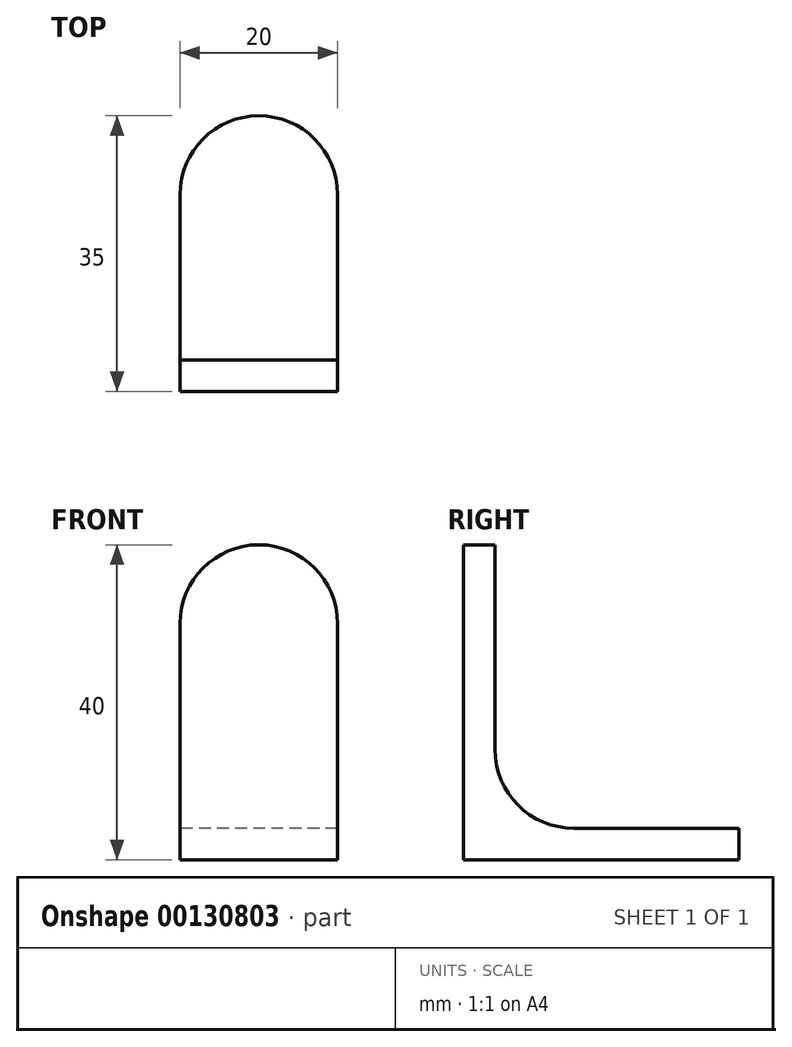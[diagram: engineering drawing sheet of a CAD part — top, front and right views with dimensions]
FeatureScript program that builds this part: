
annotation { "Feature Type Name" : "Feature", "Feature Type Description" : "" }
export const myFeature = defineFeature(function(context is Context, id is Id, definition is map)
    precondition{}
    {
        {
            var Q0;
            Q0=qCreatedBy(makeId("Right.planeOp"),FACE);
            var sketch = newSketch(context, id + "F0", { "sketchPlane" : qUnion([Q0])});
            skLineSegment(sketch, "E0.bottom", {"start": v(0, 0) * mm, "end": v(35, 0) * mm});
            skLineSegment(sketch, "E0.top", {"start": v(0, 4) * mm, "end": v(35, 4) * mm});
            skLineSegment(sketch, "E0.left", {"start": v(0, 0) * mm, "end": v(0, 4) * mm});
            skLineSegment(sketch, "E0.right", {"start": v(35, 0) * mm, "end": v(35, 4) * mm});
            skLineSegment(sketch, "E1.bottom", {"start": v(0, 0) * mm, "end": v(4, 0) * mm});
            skLineSegment(sketch, "E1.top", {"start": v(0, 40) * mm, "end": v(4, 40) * mm});
            skLineSegment(sketch, "E1.left", {"start": v(0, 0) * mm, "end": v(0, 40) * mm});
            skLineSegment(sketch, "E1.right", {"start": v(4, 0) * mm, "end": v(4, 40) * mm});
            skSolve(sketch);
        }
        {
            var Q0;
            Q0 = qSketchRegion(id + "F0", true);
            extrude(context, id + "F1", {"entities" : qUnion([Q0]), "endBound" : BoundingType.SYMMETRIC, "depth" : 20 * mm});
        }
        {
            var Q0;
            Q0=makeQuery(id+"F1.opExtrude","SWEPT_EDGE",EDGE,{"disambiguationData":[OSD([sQuery(id+"F0.wireOp",EDGE,"E0.top"),sQuery(id+"F0.wireOp",EDGE,"E1.right")])]});
            var Q1;
            Q1=makeQuery(id+"F1.opExtrude","CAP_EDGE",EDGE,{"disambiguationData":[OSD([sQuery(id+"F0.wireOp",EDGE,"E0.right")])],"isStart":false});
            var Q2;
            Q2=makeQuery(id+"F1.opExtrude","CAP_EDGE",EDGE,{"disambiguationData":[OSD([sQuery(id+"F0.wireOp",EDGE,"E0.right")])],"isStart":true});
            var Q3;
            Q3=makeQuery(id+"F1.opExtrude","CAP_EDGE",EDGE,{"disambiguationData":[OSD([sQuery(id+"F0.wireOp",EDGE,"E1.top")])],"isStart":false});
            var Q4;
            Q4=makeQuery(id+"F1.opExtrude","CAP_EDGE",EDGE,{"disambiguationData":[OSD([sQuery(id+"F0.wireOp",EDGE,"E1.top")])],"isStart":true});
            fillet(context, id + "F2", {"entities" : qUnion([Q0, Q1, Q2, Q3, Q4]), "radius" : 10 * mm, "tangentPropagation" : true, "allowEdgeOverflow" : false});
        }
    });
